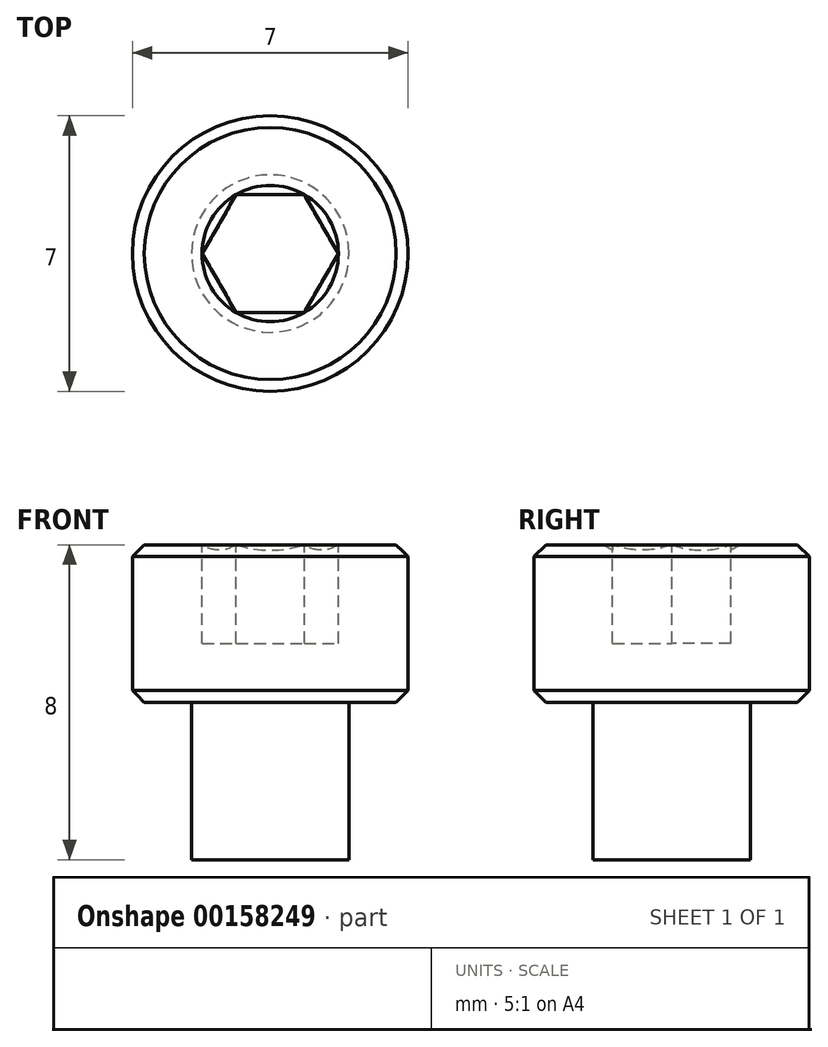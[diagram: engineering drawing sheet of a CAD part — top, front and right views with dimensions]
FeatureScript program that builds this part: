
annotation { "Feature Type Name" : "Feature", "Feature Type Description" : "" }
export const myFeature = defineFeature(function(context is Context, id is Id, definition is map)
    precondition{}
    {
        {
            var Q0;
            Q0=qCreatedBy(makeId("Front.planeOp"),FACE);
            var sketch = newSketch(context, id + "F0", { "sketchPlane" : qUnion([Q0])});
            skLineSegment(sketch, "E0", {"start": v(0, 4) * mm, "end": v(3.5, 4) * mm});
            skLineSegment(sketch, "E1", {"start": v(3.5, 4) * mm, "end": v(3.5, 0) * mm});
            skLineSegment(sketch, "E2", {"start": v(3.5, 0) * mm, "end": v(2, 0) * mm});
            skLineSegment(sketch, "E3", {"start": v(2, 0) * mm, "end": v(2, -4) * mm});
            skLineSegment(sketch, "E4", {"start": v(2, -4) * mm, "end": v(0, -4) * mm});
            skLineSegment(sketch, "E5", {"start": v(0, -4) * mm, "end": v(0, 4) * mm, "construction": true});
            skLineSegment(sketch, "E6", {"start": v(0, 4) * mm, "end": v(0, -4) * mm});
            skSolve(sketch);
        }
        {
            var Q0;
            Q0=makeQuery(id+"F0.imprint","IMPRINT",FACE,{"disambiguationData":[TD([[makeQuery(id+"F0.imprint","IMPRINT",EDGE,{"derivedFrom":sQuery(id+"F0.wireOp",EDGE,"E0")}),-1.0]])]});
            var Q1;
            Q1=sQuery(id+"F0.wireOp",EDGE,"E6");
            revolve(context, id + "F1", {"surfaceOperationType" : NewSurfaceOperationType.NEW, "entities" : qUnion([Q0]), "axis" : qUnion([Q1]), "revolveType" : RevolveType.FULL});
        }
        {
            var Q0;
            Q0=makeQuery(id+"F1.opRevolve","SWEPT_FACE",FACE,{"disambiguationData":[OSD([sQuery(id+"F0.wireOp",EDGE,"E0")])]});
            var sketch = newSketch(context, id + "F2", { "sketchPlane" : qUnion([Q0])});
            skCircle(sketch, "E7.cCircle", {"center": v(0, 0) * mm, "radius": 1.5 * mm, "construction": true});
            skLineSegment(sketch, "E7.0", {"start": v(0.87, 1.5) * mm, "end": v(1.73, 0) * mm});
            skLineSegment(sketch, "E7.1", {"start": v(1.73, 0) * mm, "end": v(0.87, -1.5) * mm});
            skLineSegment(sketch, "E7.2", {"start": v(0.87, -1.5) * mm, "end": v(-0.87, -1.5) * mm});
            skLineSegment(sketch, "E7.3", {"start": v(-0.87, -1.5) * mm, "end": v(-1.73, 0) * mm});
            skLineSegment(sketch, "E7.4", {"start": v(-1.73, 0) * mm, "end": v(-0.87, 1.5) * mm});
            skLineSegment(sketch, "E7.5", {"start": v(-0.87, 1.5) * mm, "end": v(0.87, 1.5) * mm});
            skPoint(sketch, "E7.0.midPoint", {"position": v(1.3, 0.75) * mm});
            skSolve(sketch);
        }
        {
            var Q0;
            Q0 = qSketchRegion(id + "F2", true);
            extrude(context, id + "F3", {"entities" : qUnion([Q0]), "operationType" : NewBodyOperationType.REMOVE, "oppositeDirection" : true, "depth" : 2.5 * mm});
        }
        {
            var Q0;
            Q0=qCreatedBy(makeId("Front.planeOp"),FACE);
            var sketch = newSketch(context, id + "F4", { "sketchPlane" : qUnion([Q0])});
            skArc(sketch, "E8", {"start": v(0, 10) * mm, "mid": v(-3.25, 6.75) * mm, "end": v(0, 3.5) * mm});
            skLineSegment(sketch, "E9", {"start": v(0, 6.75) * mm, "end": v(0, 0) * mm, "construction": true});
            skLineSegment(sketch, "E10", {"start": v(0, 10) * mm, "end": v(0, 3.5) * mm});
            skSolve(sketch);
        }
        {
            var Q0;
            Q0 = qSketchRegion(id + "F4", true);
            var Q1;
            Q1=sQuery(id+"F4.wireOp",EDGE,"E9");
            revolve(context, id + "F5", {"operationType" : NewBodyOperationType.REMOVE, "entities" : qUnion([Q0]), "axis" : qUnion([Q1]), "revolveType" : RevolveType.FULL, "oppositeDirection" : true});
        }
        {
            var Q0;
            Q0=makeQuery(id+"F1.opRevolve","SWEPT_EDGE",EDGE,{"disambiguationData":[OSD([sQuery(id+"F0.wireOp",EDGE,"E0"),sQuery(id+"F0.wireOp",EDGE,"E1")])]});
            var Q1;
            Q1=makeQuery(id+"F1.opRevolve","SWEPT_EDGE",EDGE,{"disambiguationData":[OSD([sQuery(id+"F0.wireOp",EDGE,"E1"),sQuery(id+"F0.wireOp",EDGE,"E2")])]});
            chamfer(context, id + "F6", {"entities" : qUnion([Q0, Q1]), "width" : .3 * mm, "tangentPropagation" : true});
        }
    });
